# Revit family: In_Wall_Carrier-Grohe-Rapid_SLX- 39602000
name_source: partatom
category: Plumbing Fixtures
units: mm (PartAtom-declared; Revit-internal decimal feet)

## family parameters
Cut with Voids When Loaded = No
Host = Face
OmniClass Number = 23.45.05.21.14
OmniClass Title = Sanitary Disposal Components
Part Type = Normal
Room Calculation Point = No
Round Connector Dimension = Use Radius
Shared = Yes

## types (1)
- 39602000
    ADA Compliant = Yes
    Assembly Code = D2030400
    Back Outlet Piping = 5 5/16"
    Back Outlet Piping Constraints = 5 5/16"
    CW Connection = Yes
    CalGreen Compliant = Yes
    Compliance Certifications = Massachusetts Plumbing Board Approved • ASSE 1002 • CSA B45.15 • CSA B125.3 • CSA B125.12 • ASME A112.6.2 • ASME A112.19.5 • ASME A112.1002
    Default Elevation = 0"
    Description = Rapid SLX 2” x 6” In-Wall Carrier
    Finish = Steel-Grohe-Powder Coated
    Floor Depth = 7 7/8"
    Floor Depth Constraint = 7 7/8"
    Flush Rate = 0.8-1.6gpf (3-6lpf)
    HW Connection = No
    Height = 44 1/2"
    Inlet Connection Diameter = 1/2"
    Installation Type = Floor Mounted
    Length = 19 7/16"
    Manufacturer = GROHE
    Material = Steel-Grohe-Powder Coated
    Model = 39602000
    Product Documentation Link = https://americanstandard.box.com
    Product Page URL = https://www.grohe.us
    Top Box Projection = 2 3/4"
    Top Box Projection Constraint = 2 3/4"
    Type Comments = For use with 6 ¼” x 7 ¾” (156 x 197mm) flush plates, please order shaft 66 791 000 (sold
separately)
    URL = https://www.grohe.us
    Vent Connection = No
    Waste Connection = Yes
    Waste Connection Diameter = 3 1/8"
    Waste Connection Height = 9 1/16"
    Width = 2"

## geometry (parser evidence)
native form markers: Sweep x3
no freeform markers — native parametric forms only
